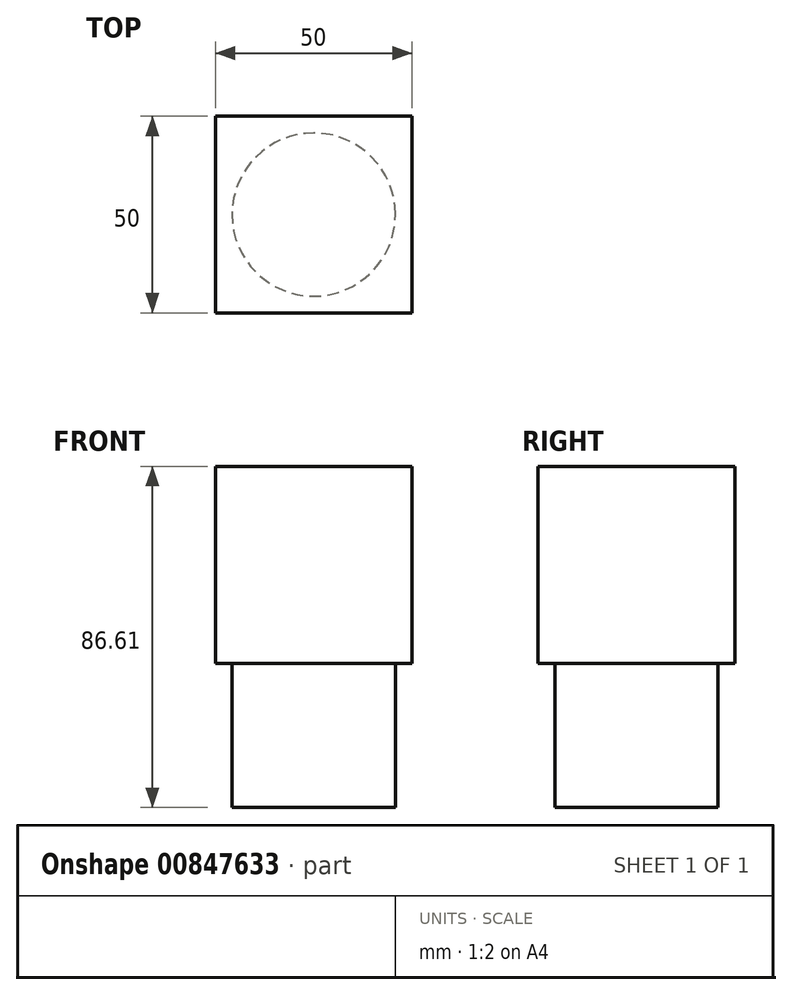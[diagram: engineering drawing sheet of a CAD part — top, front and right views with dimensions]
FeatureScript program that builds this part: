
annotation { "Feature Type Name" : "Feature", "Feature Type Description" : "" }
export const myFeature = defineFeature(function(context is Context, id is Id, definition is map)
    precondition{}
    {
        {
            var Q0;
            Q0=qCreatedBy(makeId("Top.planeOp"),FACE);
            var sketch = newSketch(context, id + "F0", { "sketchPlane" : qUnion([Q0])});
            skLineSegment(sketch, "E0.bottom", {"start": v(25, -25) * mm, "end": v(-25, -25) * mm});
            skLineSegment(sketch, "E0.top", {"start": v(25, 25) * mm, "end": v(-25, 25) * mm});
            skLineSegment(sketch, "E0.left", {"start": v(25, -25) * mm, "end": v(25, 25) * mm});
            skLineSegment(sketch, "E0.right", {"start": v(-25, -25) * mm, "end": v(-25, 25) * mm});
            skPoint(sketch, "E0.middle", {"position": v(0, 0) * mm});
            skSolve(sketch);
        }
        {
            var Q0;
            Q0 = qSketchRegion(id + "F0", true);
            extrude(context, id + "F1", {"entities" : qUnion([Q0]), "depth" : 50 * mm, "offsetDistance" : 25 * mm});
        }
        {
            var Q0;
            Q0=makeQuery(id+"F1.opExtrude","SWEPT_FACE",FACE,{"disambiguationData":[OSD([sQuery(id+"F0.wireOp",EDGE,"E0.left")])]});
            var sketch = newSketch(context, id + "F2", { "sketchPlane" : qUnion([Q0])});
            skSolve(sketch);
        }
        {
            var Q0;
            {var subQ0=sQuery(id+"F0.wireOp",EDGE,"E0.left");Q0=makeQuery(id+"F2.imprint","IMPRINT",FACE,{"disambiguationData":[TD([[makeQuery(id+"F2.imprint","IMPRINT",EDGE,{"derivedFrom":makeQuery(id+"F1.opExtrude","CAP_EDGE",EDGE,{"disambiguationData":[OSD([subQ0])],"isStart":true})}),1.0]])]});}
            extrude(context, id + "F3", {"entities" : qUnion([Q0]), "operationType" : NewBodyOperationType.ADD, "oppositeDirection" : true, "depth" : 25 * mm, "offsetDistance" : 25 * mm});
        }
        {
            var Q0;
            Q0=makeQuery(id+"F1.opExtrude","CAP_FACE",FACE,{"disambiguationData":[OSD([sQuery(id+"F0.wireOp",EDGE,"E0.bottom"),sQuery(id+"F0.wireOp",EDGE,"E0.top"),sQuery(id+"F0.wireOp",EDGE,"E0.left"),sQuery(id+"F0.wireOp",EDGE,"E0.right")])],"isStart":false});
            var sketch = newSketch(context, id + "F4", { "sketchPlane" : qUnion([Q0])});
            skCircle(sketch, "E1", {"center": v(0, 0) * mm, "radius": 20.74 * mm});
            skSolve(sketch);
        }
        {
            var Q0;
            Q0=makeQuery(id+"F4.imprint","IMPRINT",FACE,{"disambiguationData":[TD([[makeQuery(id+"F4.imprint","IMPRINT",EDGE,{"derivedFrom":sQuery(id+"F4.wireOp",EDGE,"E1")}),1.0]])]});
            extrude(context, id + "F5", {"entities" : qUnion([Q0]), "operationType" : NewBodyOperationType.ADD, "endBound" : BoundingType.THROUGH_ALL, "oppositeDirection" : true, "depth" : 25 * mm, "offsetDistance" : 25 * mm});
        }
    });
